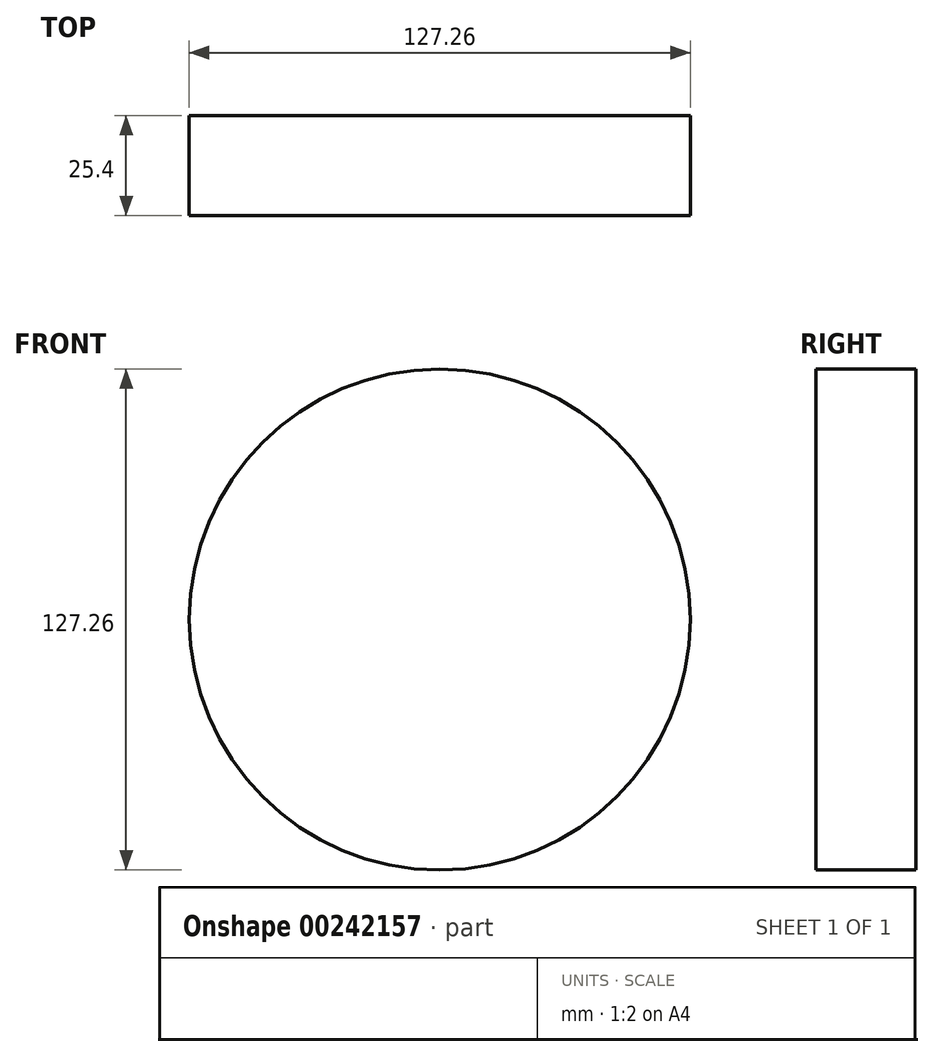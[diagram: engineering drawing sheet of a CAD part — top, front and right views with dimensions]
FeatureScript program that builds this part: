
annotation { "Feature Type Name" : "Feature", "Feature Type Description" : "" }
export const myFeature = defineFeature(function(context is Context, id is Id, definition is map)
    precondition{}
    {
        {
            var Q0;
            Q0=qCreatedBy(makeId("Front.planeOp"),FACE);
            var sketch = newSketch(context, id + "F0", { "sketchPlane" : qUnion([Q0])});
            skCircle(sketch, "E0", {"center": v(0, 0) * mm, "radius": 63.63 * mm});
            skSolve(sketch);
        }
        {
            var Q0;
            Q0=makeQuery(id+"F0.imprint","IMPRINT",FACE,{"disambiguationData":[TD([[makeQuery(id+"F0.imprint","IMPRINT",EDGE,{"derivedFrom":sQuery(id+"F0.wireOp",EDGE,"E0")}),1.0]])]});
            extrude(context, id + "F1", {"entities" : qUnion([Q0]), "depth" : 25.4 * mm});
        }
        {
            var Q0;
            Q0=makeQuery(id+"F1.opExtrude","CAP_FACE",FACE,{"disambiguationData":[OSD([sQuery(id+"F0.wireOp",EDGE,"E0")])],"isStart":true});
            var Q1;
            Q1 = qConstructionFilter(qBodyType(qCreatedBy(id + "F0" ,EDGE), BodyType.WIRE), ConstructionObject.NO);
            extrude(context, id + "F2", {"entities" : qUnion([Q0]), "bodyType" : ToolBodyType.SURFACE, "surfaceEntities" : qUnion([Q1]), "oppositeDirection" : true, "depth" : 25.4 * mm});
        }
    });
